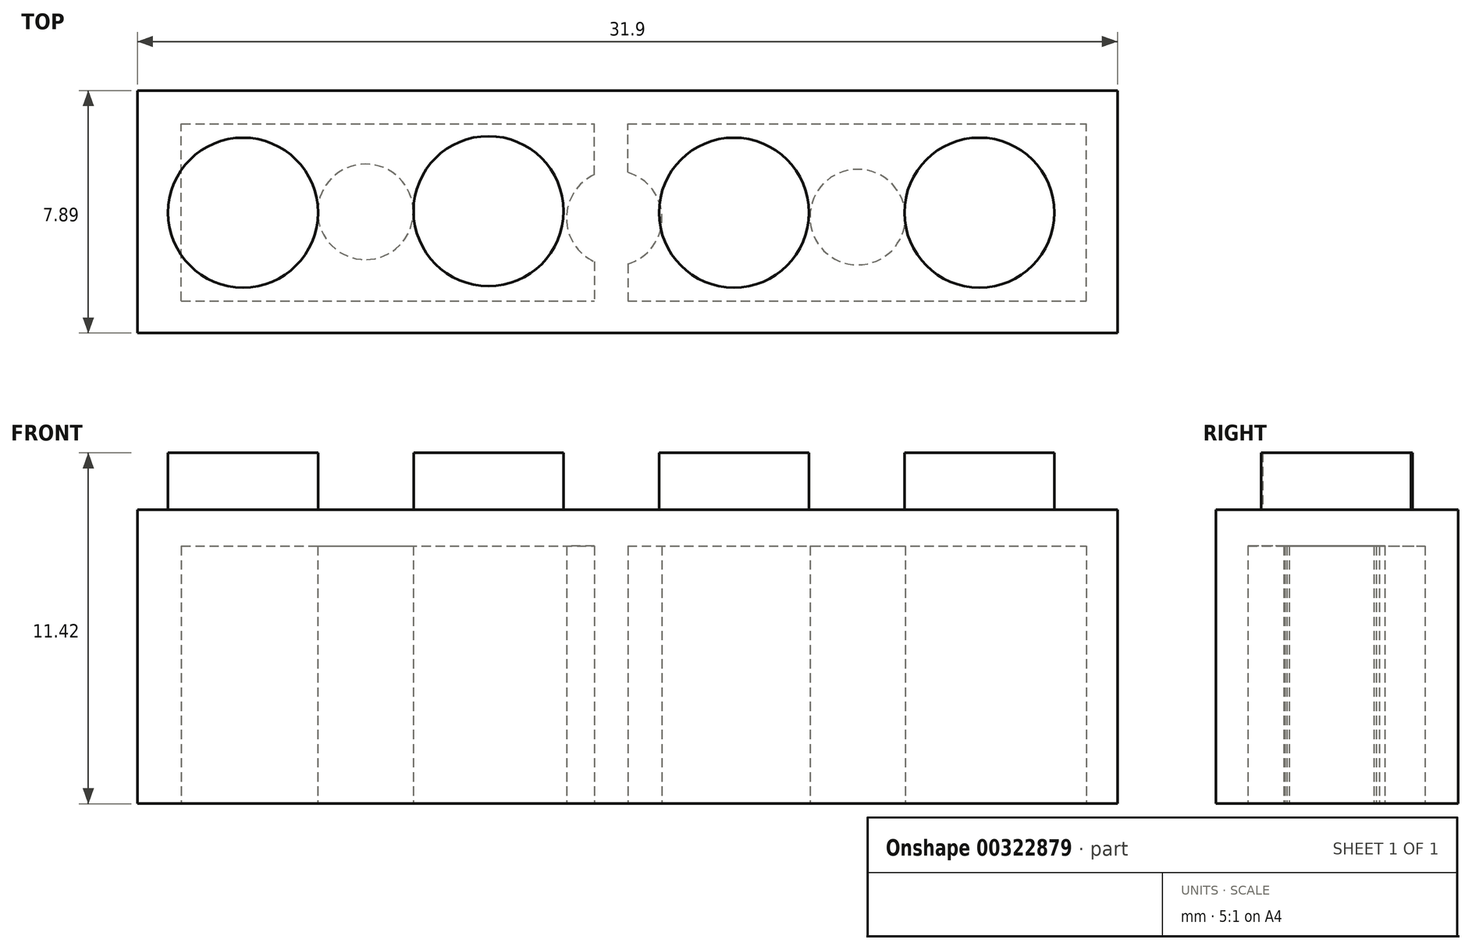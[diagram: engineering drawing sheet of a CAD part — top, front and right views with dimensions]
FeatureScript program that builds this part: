
annotation { "Feature Type Name" : "Feature", "Feature Type Description" : "" }
export const myFeature = defineFeature(function(context is Context, id is Id, definition is map)
    precondition{}
    {
        {
            var Q0;
            Q0=qCreatedBy(makeId("Front.planeOp"),FACE);
            var sketch = newSketch(context, id + "F0", { "sketchPlane" : qUnion([Q0])});
            skLineSegment(sketch, "E0.bottom", {"start": v(-26, 3.84) * mm, "end": v(5.9, 3.84) * mm});
            skLineSegment(sketch, "E0.top", {"start": v(-26, -5.73) * mm, "end": v(5.9, -5.73) * mm});
            skLineSegment(sketch, "E0.left", {"start": v(-26, 3.84) * mm, "end": v(-26, -5.73) * mm});
            skLineSegment(sketch, "E0.right", {"start": v(5.9, 3.84) * mm, "end": v(5.9, -5.73) * mm});
            skSolve(sketch);
        }
        {
            var Q0;
            Q0=makeQuery(id+"F0.imprint","IMPRINT",FACE,{"disambiguationData":[TD([[makeQuery(id+"F0.imprint","IMPRINT",EDGE,{"derivedFrom":sQuery(id+"F0.wireOp",EDGE,"E0.bottom")}),-1.0]])]});
            extrude(context, id + "F1", {"entities" : qUnion([Q0]), "depth" : 7.89 * mm});
        }
        {
            var Q0;
            Q0=makeQuery(id+"F1.opExtrude","SWEPT_FACE",FACE,{"disambiguationData":[OSD([sQuery(id+"F0.wireOp",EDGE,"E0.bottom")])]});
            var sketch = newSketch(context, id + "F2", { "sketchPlane" : qUnion([Q0])});
            skCircle(sketch, "E1", {"center": v(-22.56, -3.97) * mm, "radius": 2.44 * mm});
            skCircle(sketch, "E2", {"center": v(-14.57, -3.92) * mm, "radius": 2.44 * mm});
            skCircle(sketch, "E3", {"center": v(-6.58, -3.97) * mm, "radius": 2.44 * mm});
            skCircle(sketch, "E4", {"center": v(1.4, -3.97) * mm, "radius": 2.44 * mm});
            skSolve(sketch);
        }
        {
            var Q0;
            Q0 = qSketchRegion(id + "F2", true);
            extrude(context, id + "F3", {"entities" : qUnion([Q0]), "operationType" : NewBodyOperationType.ADD, "depth" : 1.85 * mm});
        }
        {
            var Q0;
            Q0=makeQuery(id+"F1.opExtrude","SWEPT_FACE",FACE,{"disambiguationData":[OSD([sQuery(id+"F0.wireOp",EDGE,"E0.top")])]});
            var sketch = newSketch(context, id + "F4", { "sketchPlane" : qUnion([Q0])});
            skLineSegment(sketch, "E5.bottom", {"start": v(-24.57, 6.84) * mm, "end": v(4.9, 6.84) * mm});
            skLineSegment(sketch, "E5.top", {"start": v(-24.57, 1.08) * mm, "end": v(4.9, 1.08) * mm});
            skLineSegment(sketch, "E5.left", {"start": v(-24.57, 6.84) * mm, "end": v(-24.57, 1.08) * mm});
            skLineSegment(sketch, "E5.right", {"start": v(4.9, 6.84) * mm, "end": v(4.9, 1.08) * mm});
            skCircle(sketch, "E6", {"center": v(-18.57, 3.95) * mm, "radius": 1.55 * mm});
            skPoint(sketch, "E6.centerSnap0", {"position": v(-26, 3.94) * mm});
            skCircle(sketch, "E7", {"center": v(-10.48, 4.15) * mm, "radius": 1.55 * mm});
            skCircle(sketch, "E8", {"center": v(-2.55, 4.11) * mm, "radius": 1.55 * mm});
            skLineSegment(sketch, "E9", {"start": v(-11.12, 2.73) * mm, "end": v(-11.12, 1.08) * mm});
            skLineSegment(sketch, "E10", {"start": v(-10.04, 2.66) * mm, "end": v(-10.04, 1.08) * mm});
            skLineSegment(sketch, "E11", {"start": v(-11.12, 5.57) * mm, "end": v(-11.12, 6.84) * mm});
            skLineSegment(sketch, "E12", {"start": v(-10.04, 5.64) * mm, "end": v(-10.04, 6.84) * mm});
            skSolve(sketch);
        }
        {
            var Q0;
            {var subQ0=sQuery(id+"F4.wireOp",EDGE,"E5.left");Q0=makeQuery(id+"F4.imprint","IMPRINT",FACE,{"disambiguationData":[TD([[makeQuery(id+"F4.imprint","IMPRINT",EDGE,{"derivedFrom":subQ0}),1.0]])]});}
            var Q1;
            {var subQ0=sQuery(id+"F4.wireOp",EDGE,"E5.right");Q1=makeQuery(id+"F4.imprint","IMPRINT",FACE,{"disambiguationData":[TD([[makeQuery(id+"F4.imprint","IMPRINT",EDGE,{"derivedFrom":subQ0}),-1.0]])]});}
            extrude(context, id + "F5", {"entities" : qUnion([Q0, Q1]), "operationType" : NewBodyOperationType.REMOVE, "oppositeDirection" : true, "depth" : 8.38 * mm});
        }
    });
